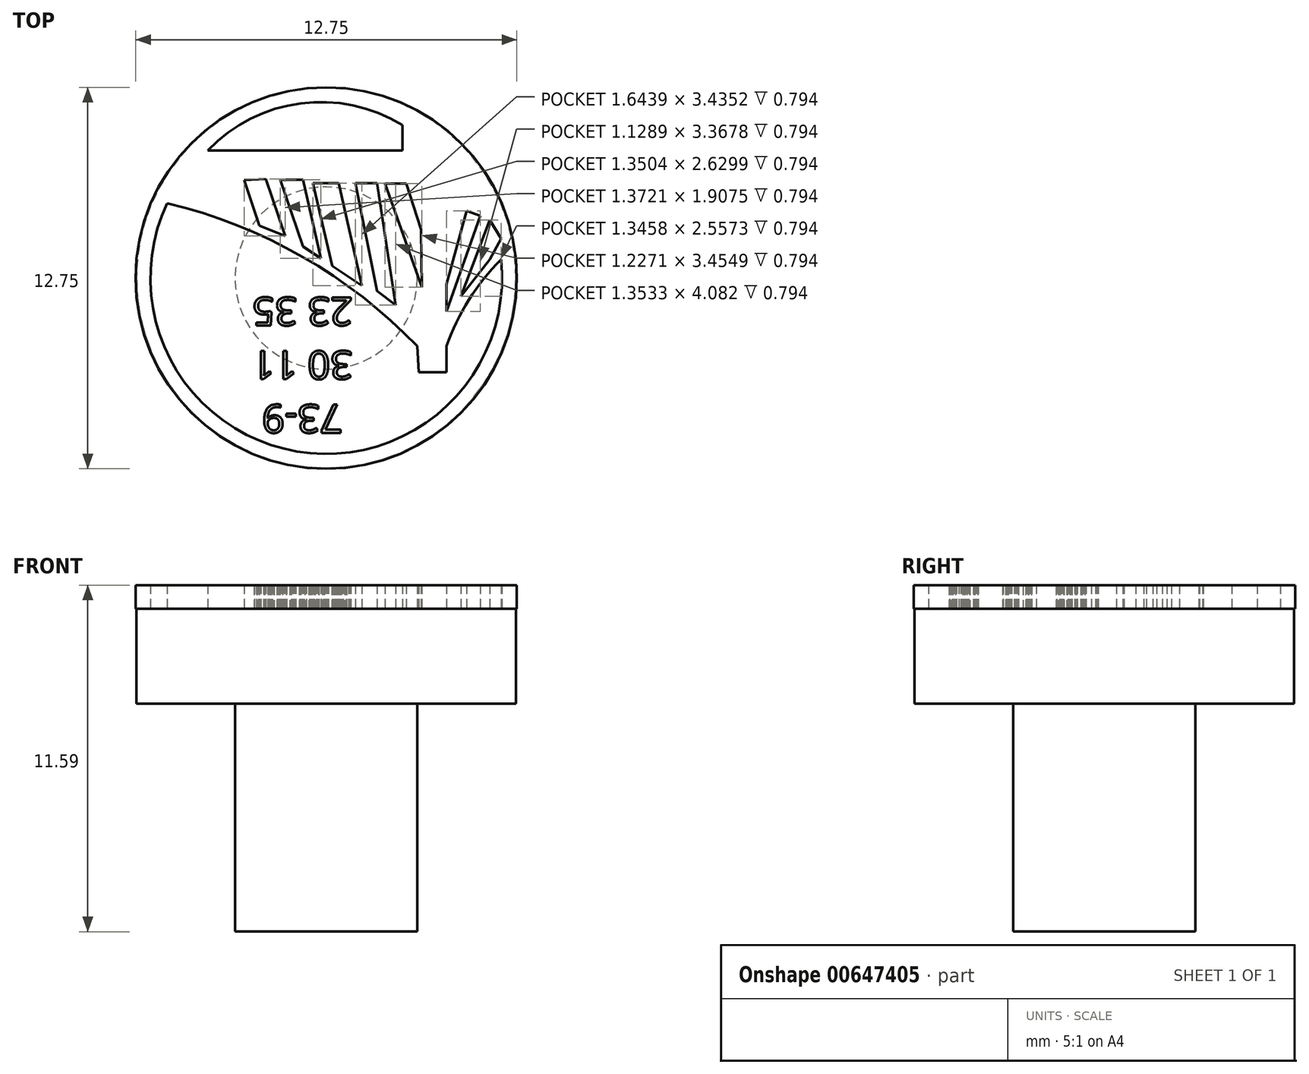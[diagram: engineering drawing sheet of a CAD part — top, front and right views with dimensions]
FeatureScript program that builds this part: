
annotation { "Feature Type Name" : "Feature", "Feature Type Description" : "" }
export const myFeature = defineFeature(function(context is Context, id is Id, definition is map)
    precondition{}
    {
        {
            var Q0;
            Q0=qCreatedBy(makeId("Top.planeOp"),FACE);
            var sketch = newSketch(context, id + "F0", { "sketchPlane" : qUnion([Q0])});
            skArc(sketch, "E0", {"start": v(4.56, -0.94) * mm, "mid": v(3.5, -2.28) * mm, "end": v(2.74, -3.83) * mm});
            skLineSegment(sketch, "E1", {"start": v(2.74, -3.83) * mm, "end": v(2.74, -4.7) * mm});
            skLineSegment(sketch, "E2", {"start": v(2.74, -4.7) * mm, "end": v(1.8, -4.7) * mm});
            skLineSegment(sketch, "E3", {"start": v(1.8, -4.7) * mm, "end": v(1.76, -3.83) * mm});
            skArc(sketch, "E4", {"start": v(1.76, -3.83) * mm, "mid": v(-2.08, -0.84) * mm, "end": v(-6.6, 0.95) * mm});
            skArc(sketch, "E5", {"start": v(-6.6, 0.95) * mm, "mid": v(-2.26, -7.35) * mm, "end": v(4.56, -0.94) * mm});
            skCircle(sketch, "E6", {"center": v(-1.29, -1.55) * mm, "radius": 6.38 * mm});
            skLineSegment(sketch, "E7", {"start": v(-5.25, 2.71) * mm, "end": v(1.27, 2.71) * mm});
            skLineSegment(sketch, "E8", {"start": v(1.27, 2.71) * mm, "end": v(1.27, 3.56) * mm});
            skArc(sketch, "E9", {"start": v(1.27, 3.56) * mm, "mid": v(-2.14, 4.29) * mm, "end": v(-5.25, 2.71) * mm});
            skLineSegment(sketch, "E10", {"start": v(4.56, -0.24) * mm, "end": v(4.2, -0.94) * mm});
            skLineSegment(sketch, "E11", {"start": v(4.2, 0.39) * mm, "end": v(4.56, -0.24) * mm});
            skLineSegment(sketch, "E12", {"start": v(3.4, 0.7) * mm, "end": v(3.87, 0.53) * mm});
            skPoint(sketch, "E13.endSnap0", {"position": v(3.5, -2.29) * mm});
            skLineSegment(sketch, "E14", {"start": v(-1.47, -0.9) * mm, "end": v(-2.06, 1.73) * mm});
            skLineSegment(sketch, "E15", {"start": v(-2.06, 1.73) * mm, "end": v(-2.82, 1.73) * mm});
            skLineSegment(sketch, "E16", {"start": v(-2.82, 1.73) * mm, "end": v(-2.06, -0.5) * mm});
            skLineSegment(sketch, "E17", {"start": v(-2.06, -0.5) * mm, "end": v(-1.47, -0.9) * mm});
            skLineSegment(sketch, "E18", {"start": v(-2.66, -0.15) * mm, "end": v(-3.3, 1.76) * mm});
            skLineSegment(sketch, "E19", {"start": v(-3.3, 1.76) * mm, "end": v(-4.04, 1.72) * mm});
            skLineSegment(sketch, "E20", {"start": v(-4.04, 1.72) * mm, "end": v(-3.52, 0.2) * mm});
            skLineSegment(sketch, "E21", {"start": v(-3.52, 0.2) * mm, "end": v(-2.66, -0.15) * mm});
            skLineSegment(sketch, "E22", {"start": v(-4.64, 1.72) * mm, "end": v(-5.63, 1.68) * mm});
            skLineSegment(sketch, "E23", {"start": v(-5.63, 1.68) * mm, "end": v(-5.1, 0.78) * mm});
            skLineSegment(sketch, "E24", {"start": v(-5.1, 0.78) * mm, "end": v(-4.2, 0.64) * mm});
            skLineSegment(sketch, "E25", {"start": v(-4.2, 0.64) * mm, "end": v(-4.54, 1.68) * mm});
            skLineSegment(sketch, "E26", {"start": v(-1.73, 1.62) * mm, "end": v(-0.87, 1.62) * mm});
            skLineSegment(sketch, "E27", {"start": v(-0.87, 1.62) * mm, "end": v(-0.09, -1.81) * mm});
            skLineSegment(sketch, "E28", {"start": v(-0.09, -1.81) * mm, "end": v(-1.09, -1.15) * mm});
            skLineSegment(sketch, "E29", {"start": v(-1.09, -1.15) * mm, "end": v(-1.73, 1.62) * mm});
            skLineSegment(sketch, "E30", {"start": v(-0.31, 1.62) * mm, "end": v(0.42, 1.62) * mm});
            skLineSegment(sketch, "E31", {"start": v(0.42, 1.62) * mm, "end": v(1.04, -2.46) * mm});
            skLineSegment(sketch, "E32", {"start": v(1.04, -2.46) * mm, "end": v(0.42, -2) * mm});
            skLineSegment(sketch, "E33", {"start": v(0.42, -2) * mm, "end": v(-0.31, 1.62) * mm});
            skLineSegment(sketch, "E34", {"start": v(1.91, -1.85) * mm, "end": v(0.69, 1.6) * mm});
            skLineSegment(sketch, "E35", {"start": v(0.69, 1.6) * mm, "end": v(1.4, 1.6) * mm});
            skLineSegment(sketch, "E36", {"start": v(1.4, 1.6) * mm, "end": v(1.88, 0.07) * mm});
            skLineSegment(sketch, "E37", {"start": v(1.91, -1.85) * mm, "end": v(1.88, 0.07) * mm});
            skLineSegment(sketch, "E38", {"start": v(4.2, 0.39) * mm, "end": v(3.22, -2.17) * mm});
            skLineSegment(sketch, "E39", {"start": v(3.22, -2.17) * mm, "end": v(4.2, -0.94) * mm});
            skLineSegment(sketch, "E40", {"start": v(2.74, -2.68) * mm, "end": v(2.74, -1.76) * mm});
            skLineSegment(sketch, "E41", {"start": v(3.87, 0.53) * mm, "end": v(2.74, -2.68) * mm});
            skLineSegment(sketch, "E42", {"start": v(3.41, 0.7) * mm, "end": v(2.74, -1.76) * mm});
            skSolve(sketch);
        }
        {
            var Q0;
            Q0=makeQuery(id+"F0.imprint","IMPRINT",FACE,{"disambiguationData":[TD([[makeQuery(id+"F0.imprint","IMPRINT",EDGE,{"derivedFrom":sQuery(id+"F0.wireOp",EDGE,"E0")}),-1.0]])]});
            extrude(context, id + "F1", {"entities" : qUnion([Q0]), "depth" : 0.8 * mm, "offsetDistance" : 25.4 * mm});
        }
        {
            var Q0;
            Q0=makeQuery(id+"F1.opExtrude","CAP_FACE",FACE,{"disambiguationData":[OSD([sQuery(id+"F0.wireOp",EDGE,"E0"),sQuery(id+"F0.wireOp",EDGE,"E1"),sQuery(id+"F0.wireOp",EDGE,"E2"),sQuery(id+"F0.wireOp",EDGE,"E3"),sQuery(id+"F0.wireOp",EDGE,"E4"),sQuery(id+"F0.wireOp",EDGE,"E5"),sQuery(id+"F0.wireOp",EDGE,"E6"),sQuery(id+"F0.wireOp",EDGE,"E7"),sQuery(id+"F0.wireOp",EDGE,"E8"),sQuery(id+"F0.wireOp",EDGE,"E9"),sQuery(id+"F0.wireOp",EDGE,"E10"),sQuery(id+"F0.wireOp",EDGE,"E11"),sQuery(id+"F0.wireOp",EDGE,"E12"),sQuery(id+"F0.wireOp",EDGE,"E14"),sQuery(id+"F0.wireOp",EDGE,"E15"),sQuery(id+"F0.wireOp",EDGE,"E16"),sQuery(id+"F0.wireOp",EDGE,"E17"),sQuery(id+"F0.wireOp",EDGE,"E18"),sQuery(id+"F0.wireOp",EDGE,"E19"),sQuery(id+"F0.wireOp",EDGE,"E20"),sQuery(id+"F0.wireOp",EDGE,"E21"),sQuery(id+"F0.wireOp",EDGE,"E26"),sQuery(id+"F0.wireOp",EDGE,"E27"),sQuery(id+"F0.wireOp",EDGE,"E28"),sQuery(id+"F0.wireOp",EDGE,"E29"),sQuery(id+"F0.wireOp",EDGE,"E30"),sQuery(id+"F0.wireOp",EDGE,"E31"),sQuery(id+"F0.wireOp",EDGE,"E32"),sQuery(id+"F0.wireOp",EDGE,"E33"),sQuery(id+"F0.wireOp",EDGE,"E34"),sQuery(id+"F0.wireOp",EDGE,"E35"),sQuery(id+"F0.wireOp",EDGE,"E36"),sQuery(id+"F0.wireOp",EDGE,"E37"),sQuery(id+"F0.wireOp",EDGE,"E38"),sQuery(id+"F0.wireOp",EDGE,"E39"),sQuery(id+"F0.wireOp",EDGE,"E40"),sQuery(id+"F0.wireOp",EDGE,"E41"),sQuery(id+"F0.wireOp",EDGE,"E42")])],"isStart":true});
            var sketch = newSketch(context, id + "F2", { "sketchPlane" : qUnion([Q0])});
            skCircle(sketch, "E43", {"center": v(-1.29, 1.55) * mm, "radius": 6.35 * mm});
            skSolve(sketch);
        }
        {
            var Q0;
            Q0=makeQuery(id+"F2.imprint","IMPRINT",FACE,{"disambiguationData":[TD([[makeQuery(id+"F2.imprint","IMPRINT",EDGE,{"derivedFrom":makeQuery(id+"F1.opExtrude","CAP_EDGE",EDGE,{"disambiguationData":[OSD([sQuery(id+"F0.wireOp",EDGE,"E0")])],"isStart":true})}),-1.0]])]});
            var Q1;
            Q1=makeQuery(id+"F2.imprint","IMPRINT",FACE,{"disambiguationData":[TD([[makeQuery(id+"F2.imprint","IMPRINT",EDGE,{"derivedFrom":sQuery(id+"F2.wireOp",EDGE,"E43")}),1.0]])]});
            var Q2;
            Q2=makeQuery(id+"F2.imprint","IMPRINT",FACE,{"disambiguationData":[TD([[makeQuery(id+"F2.imprint","IMPRINT",EDGE,{"derivedFrom":makeQuery(id+"F1.opExtrude","CAP_EDGE",EDGE,{"disambiguationData":[OSD([sQuery(id+"F0.wireOp",EDGE,"E7")])],"isStart":true})}),-1.0]])]});
            var Q3;
            Q3=makeQuery(id+"F2.imprint","IMPRINT",FACE,{"disambiguationData":[TD([[makeQuery(id+"F2.imprint","IMPRINT",EDGE,{"derivedFrom":makeQuery(id+"F1.opExtrude","CAP_EDGE",EDGE,{"disambiguationData":[OSD([sQuery(id+"F0.wireOp",EDGE,"E18")])],"isStart":true})}),-1.0]])]});
            var Q4;
            Q4=makeQuery(id+"F2.imprint","IMPRINT",FACE,{"disambiguationData":[TD([[makeQuery(id+"F2.imprint","IMPRINT",EDGE,{"derivedFrom":makeQuery(id+"F1.opExtrude","CAP_EDGE",EDGE,{"disambiguationData":[OSD([sQuery(id+"F0.wireOp",EDGE,"E14")])],"isStart":true})}),-1.0]])]});
            var Q5;
            Q5=makeQuery(id+"F2.imprint","IMPRINT",FACE,{"disambiguationData":[TD([[makeQuery(id+"F2.imprint","IMPRINT",EDGE,{"derivedFrom":makeQuery(id+"F1.opExtrude","CAP_EDGE",EDGE,{"disambiguationData":[OSD([sQuery(id+"F0.wireOp",EDGE,"E26")])],"isStart":true})}),1.0]])]});
            var Q6;
            Q6=makeQuery(id+"F2.imprint","IMPRINT",FACE,{"disambiguationData":[TD([[makeQuery(id+"F2.imprint","IMPRINT",EDGE,{"derivedFrom":makeQuery(id+"F1.opExtrude","CAP_EDGE",EDGE,{"disambiguationData":[OSD([sQuery(id+"F0.wireOp",EDGE,"E30")])],"isStart":true})}),1.0]])]});
            var Q7;
            Q7=makeQuery(id+"F2.imprint","IMPRINT",FACE,{"disambiguationData":[TD([[makeQuery(id+"F2.imprint","IMPRINT",EDGE,{"derivedFrom":makeQuery(id+"F1.opExtrude","CAP_EDGE",EDGE,{"disambiguationData":[OSD([sQuery(id+"F0.wireOp",EDGE,"E34")])],"isStart":true})}),1.0]])]});
            var Q8;
            Q8=makeQuery(id+"F2.imprint","IMPRINT",FACE,{"disambiguationData":[TD([[makeQuery(id+"F2.imprint","IMPRINT",EDGE,{"derivedFrom":makeQuery(id+"F1.opExtrude","CAP_EDGE",EDGE,{"disambiguationData":[OSD([sQuery(id+"F0.wireOp",EDGE,"E12")])],"isStart":true})}),1.0]])]});
            var Q9;
            Q9=makeQuery(id+"F2.imprint","IMPRINT",FACE,{"disambiguationData":[TD([[makeQuery(id+"F2.imprint","IMPRINT",EDGE,{"derivedFrom":makeQuery(id+"F1.opExtrude","CAP_EDGE",EDGE,{"disambiguationData":[OSD([sQuery(id+"F0.wireOp",EDGE,"E10")])],"isStart":true})}),1.0]])]});
            extrude(context, id + "F3", {"entities" : qUnion([Q0, Q1, Q2, Q3, Q4, Q5, Q6, Q7, Q8, Q9]), "operationType" : NewBodyOperationType.ADD, "depth" : 3.17 * mm, "offsetDistance" : 25.4 * mm});
        }
        {
            var Q0;
            Q0=makeQuery(id+"F3.boolean.opBoolean","SPLIT",FACE,{"disambiguationData":[TD([makeQuery(id+"F1.opExtrude","SWEPT_FACE",FACE,{"disambiguationData":[OSD([sQuery(id+"F0.wireOp",EDGE,"E0")])]})])],"derivedFrom":makeQuery(id+"F3.opExtrude","CAP_FACE",FACE,{"disambiguationData":[OSD([sQuery(id+"F2.wireOp",EDGE,"E43")])],"isStart":true})});
            var sketch = newSketch(context, id + "F4", { "sketchPlane" : qUnion([Q0])});
            skText(sketch, "E44", { "text": " 73-9\n30 11\n23 35", "fontName": "NotoSans-Regular.ttf"});
            const initialGuessF4  = {"E44": [-0.0004, -0.00579, -1, 0, 0.00095]};
            skSetInitialGuess(sketch, initialGuessF4);
            skSolve(sketch);
        }
        {
            var Q0;
            Q0 = qSketchRegion(id + "F4", true);
            extrude(context, id + "F5", {"entities" : qUnion([Q0]), "operationType" : NewBodyOperationType.ADD, "depth" : 0.8 * mm, "offsetDistance" : 25.4 * mm});
        }
        {
            var Q0;
            Q0=makeQuery(id+"F3.opExtrude","CAP_FACE",FACE,{"disambiguationData":[OSD([sQuery(id+"F2.wireOp",EDGE,"E43")])],"isStart":false});
            var sketch = newSketch(context, id + "F6", { "sketchPlane" : qUnion([Q0])});
            skCircle(sketch, "E45", {"center": v(-1.29, 1.55) * mm, "radius": 3.05 * mm});
            skSolve(sketch);
        }
        {
            var Q0;
            Q0=makeQuery(id+"F6.imprint","IMPRINT",FACE,{"disambiguationData":[TD([[makeQuery(id+"F6.imprint","IMPRINT",EDGE,{"derivedFrom":sQuery(id+"F6.wireOp",EDGE,"E45")}),1.0]])]});
            extrude(context, id + "F7", {"entities" : qUnion([Q0]), "operationType" : NewBodyOperationType.ADD, "depth" : 7.62 * mm, "offsetDistance" : 25.4 * mm});
        }
    });
